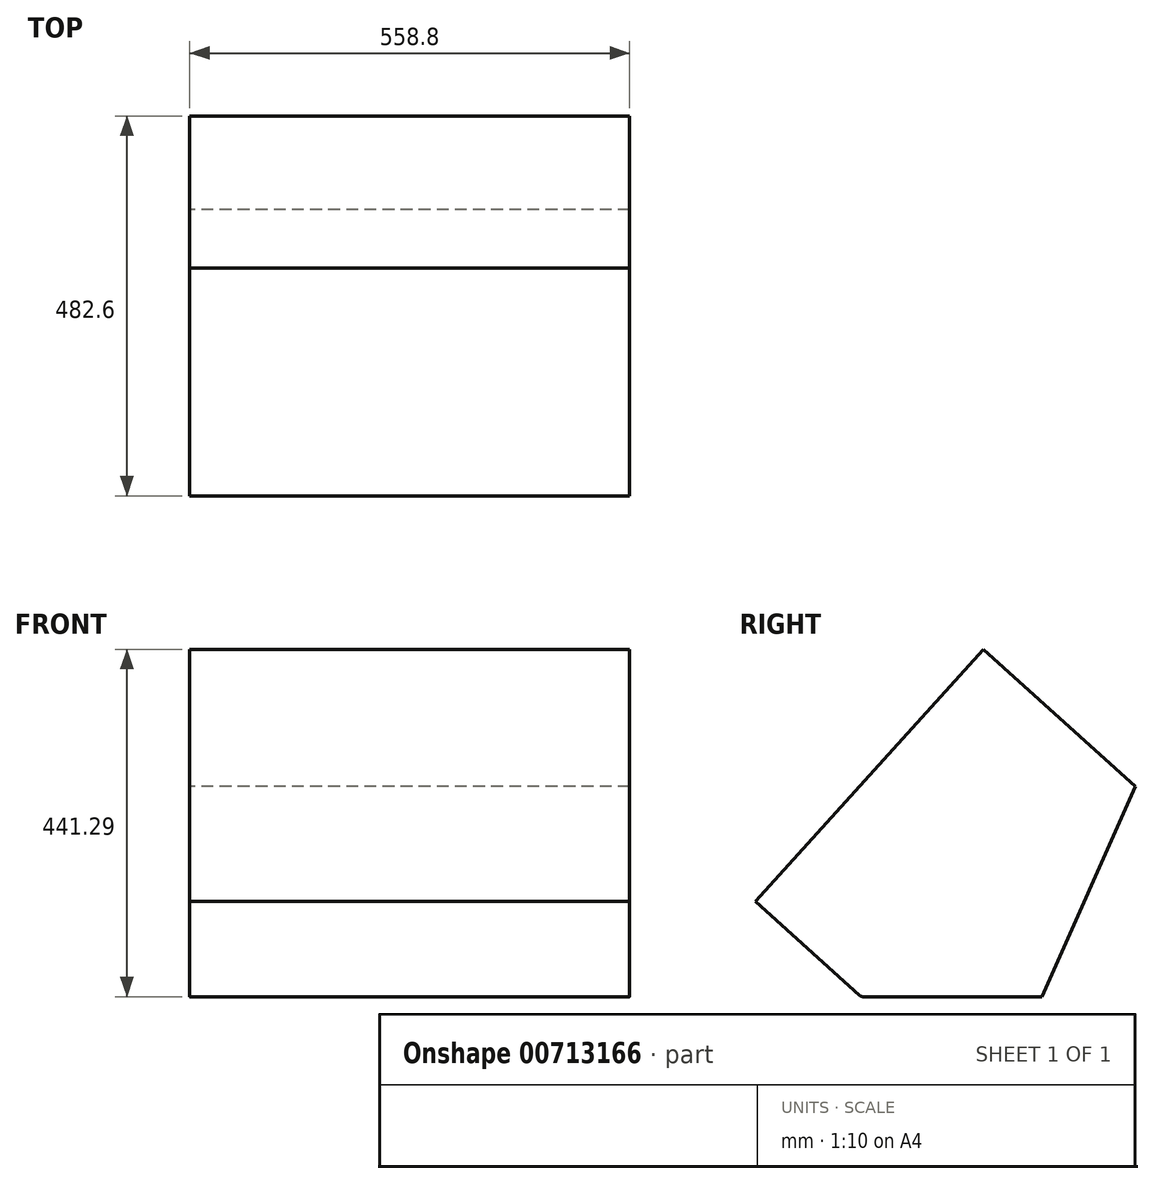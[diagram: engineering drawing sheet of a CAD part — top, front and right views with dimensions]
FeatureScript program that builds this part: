
annotation { "Feature Type Name" : "Feature", "Feature Type Description" : "" }
export const myFeature = defineFeature(function(context is Context, id is Id, definition is map)
    precondition{}
    {
        {
            var Q0;
            Q0=qCreatedBy(makeId("Right.planeOp"),FACE);
            var sketch = newSketch(context, id + "F0", { "sketchPlane" : qUnion([Q0])});
            skLineSegment(sketch, "E0", {"start": v(0, 0) * mm, "end": v(-203.2, 0) * mm});
            skLineSegment(sketch, "E1", {"start": v(-207.46, 1.64) * mm, "end": v(-339.43, 120.78) * mm});
            skLineSegment(sketch, "E2", {"start": v(-339.43, 120.78) * mm, "end": v(-50.08, 441.3) * mm});
            skLineSegment(sketch, "E3", {"start": v(-50.08, 441.3) * mm, "end": v(143.17, 266.83) * mm});
            skLineSegment(sketch, "E4", {"start": v(143.17, 266.83) * mm, "end": v(24.33, 0) * mm});
            skLineSegment(sketch, "E5", {"start": v(0, 0) * mm, "end": v(24.33, 0) * mm});
            skPoint(sketch, "E6.visualSharp", {"position": v(-205.64, 0) * mm});
            skArc(sketch, "E6.filletArc", {"start": v(-207.46, 1.64) * mm, "mid": v(-205.48, 0.42) * mm, "end": v(-203.2, 0) * mm});
            skSolve(sketch);
        }
        {
            var Q0;
            Q0 = qSketchRegion(id + "F0", true);
            extrude(context, id + "F1", {"entities" : qUnion([Q0]), "depth" : 558.8 * mm, "offsetDistance" : 25.4 * mm});
        }
    });
